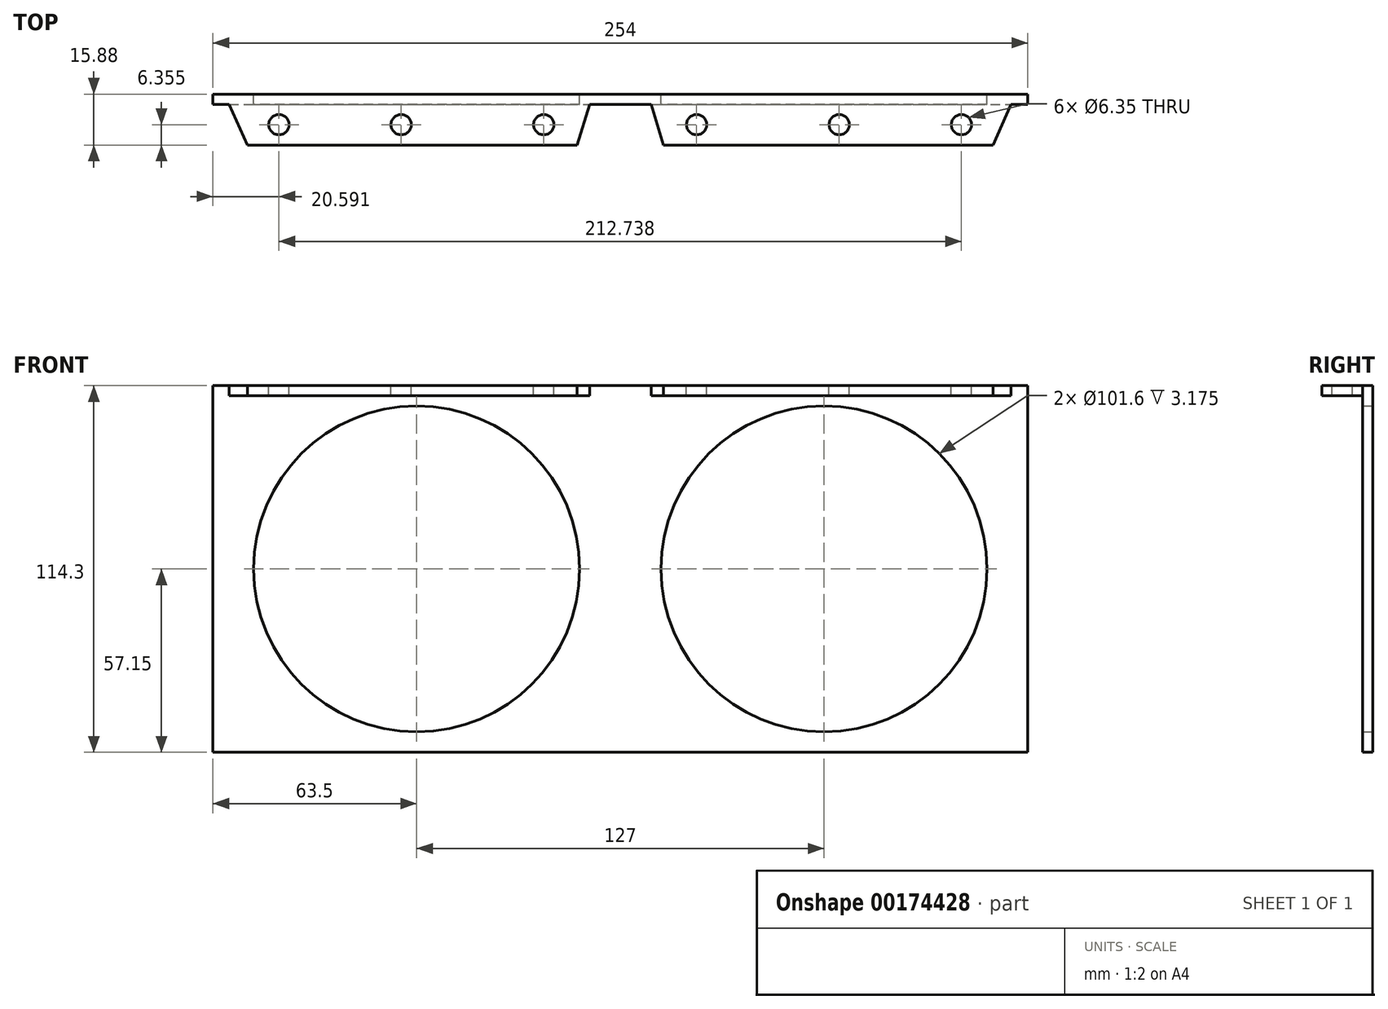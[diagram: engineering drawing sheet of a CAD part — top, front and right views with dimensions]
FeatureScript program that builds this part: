
annotation { "Feature Type Name" : "Feature", "Feature Type Description" : "" }
export const myFeature = defineFeature(function(context is Context, id is Id, definition is map)
    precondition{}
    {
        {
            var Q0;
            Q0=qCreatedBy(makeId("Front.planeOp"),FACE);
            var sketch = newSketch(context, id + "F0", { "sketchPlane" : qUnion([Q0])});
            skLineSegment(sketch, "E0.bottom", {"start": v(-127, -57.15) * mm, "end": v(127, -57.15) * mm});
            skLineSegment(sketch, "E0.top", {"start": v(-127, 57.15) * mm, "end": v(127, 57.15) * mm});
            skLineSegment(sketch, "E0.left", {"start": v(-127, -57.15) * mm, "end": v(-127, 57.15) * mm});
            skLineSegment(sketch, "E0.right", {"start": v(127, -57.15) * mm, "end": v(127, 57.15) * mm});
            skPoint(sketch, "E0.middle", {"position": v(0, 0) * mm});
            skCircle(sketch, "E1", {"center": v(63.5, 0) * mm, "radius": 50.8 * mm});
            skCircle(sketch, "E2", {"center": v(-63.5, 0) * mm, "radius": 50.8 * mm});
            skSolve(sketch);
        }
        {
            var Q0;
            Q0 = qSketchRegion(id + "F0", true);
            extrude(context, id + "F1", {"entities" : qUnion([Q0]), "depth" : 3.17 * mm});
        }
        {
            var Q0;
            Q0=makeQuery(id+"F1.opExtrude","CAP_FACE",FACE,{"disambiguationData":[OSD([sQuery(id+"F0.wireOp",EDGE,"E0.bottom"),sQuery(id+"F0.wireOp",EDGE,"E0.top"),sQuery(id+"F0.wireOp",EDGE,"E0.left"),sQuery(id+"F0.wireOp",EDGE,"E0.right"),sQuery(id+"F0.wireOp",EDGE,"E1"),sQuery(id+"F0.wireOp",EDGE,"E2")])],"isStart":false});
            var sketch = newSketch(context, id + "F2", { "sketchPlane" : qUnion([Q0])});
            skPoint(sketch, "E3", {"position": v(-122.01, 57.15) * mm});
            skPoint(sketch, "E4", {"position": v(-9.5, 57.15) * mm});
            skPoint(sketch, "E5", {"position": v(9.59, 57.15) * mm});
            skPoint(sketch, "E6", {"position": v(121.82, 57.15) * mm});
            skLineSegment(sketch, "E7.bottom", {"start": v(-122.01, 57.15) * mm, "end": v(-9.5, 57.15) * mm});
            skLineSegment(sketch, "E7.top", {"start": v(-122.01, 53.98) * mm, "end": v(-9.5, 53.98) * mm});
            skLineSegment(sketch, "E7.left", {"start": v(-122.01, 57.15) * mm, "end": v(-122.01, 53.98) * mm});
            skLineSegment(sketch, "E7.right", {"start": v(-9.5, 57.15) * mm, "end": v(-9.5, 53.98) * mm});
            skLineSegment(sketch, "E8.bottom", {"start": v(9.59, 57.15) * mm, "end": v(121.82, 57.15) * mm});
            skLineSegment(sketch, "E8.top", {"start": v(9.59, 53.98) * mm, "end": v(121.82, 53.98) * mm});
            skLineSegment(sketch, "E8.left", {"start": v(9.59, 57.15) * mm, "end": v(9.59, 53.98) * mm});
            skLineSegment(sketch, "E8.right", {"start": v(121.82, 57.15) * mm, "end": v(121.82, 53.98) * mm});
            skSolve(sketch);
        }
        {
            var Q0;
            Q0 = qSketchRegion(id + "F2", true);
            extrude(context, id + "F3", {"entities" : qUnion([Q0]), "operationType" : NewBodyOperationType.ADD, "depth" : 12.7 * mm, "offsetDistance" : 25.4 * mm});
        }
        {
            var Q0;
            Q0=makeQuery(id+"F3.boolean.opBoolean","MERGE",FACE,{"derivedFrom":[makeQuery(id+"F1.opExtrude","SWEPT_FACE",FACE,{"disambiguationData":[OSD([sQuery(id+"F0.wireOp",EDGE,"E0.top")])]}),makeQuery(id+"F3.opExtrude","SWEPT_FACE",FACE,{"disambiguationData":[OSD([sQuery(id+"F2.wireOp",EDGE,"E7.bottom")])]}),makeQuery(id+"F3.opExtrude","SWEPT_FACE",FACE,{"disambiguationData":[OSD([sQuery(id+"F2.wireOp",EDGE,"E8.bottom")])]})]});
            var sketch = newSketch(context, id + "F4", { "sketchPlane" : qUnion([Q0])});
            skLineSegment(sketch, "E9", {"start": v(-122.01, -3.18) * mm, "end": v(-116.2, -15.88) * mm});
            skLineSegment(sketch, "E10", {"start": v(-116.2, -15.88) * mm, "end": v(-122.01, -15.88) * mm});
            skLineSegment(sketch, "E11", {"start": v(-122.01, -15.88) * mm, "end": v(-122.01, -3.18) * mm});
            skLineSegment(sketch, "E12", {"start": v(-9.5, -3.18) * mm, "end": v(-13.46, -15.88) * mm});
            skLineSegment(sketch, "E13", {"start": v(-13.46, -15.88) * mm, "end": v(-9.5, -15.88) * mm});
            skLineSegment(sketch, "E14", {"start": v(-9.5, -15.88) * mm, "end": v(-9.5, -3.18) * mm});
            skLineSegment(sketch, "E15", {"start": v(9.59, -3.17) * mm, "end": v(13.48, -15.88) * mm});
            skLineSegment(sketch, "E16", {"start": v(13.48, -15.88) * mm, "end": v(9.59, -15.88) * mm});
            skLineSegment(sketch, "E17", {"start": v(9.59, -15.88) * mm, "end": v(9.59, -3.17) * mm});
            skLineSegment(sketch, "E18", {"start": v(121.82, -15.88) * mm, "end": v(116.24, -15.88) * mm});
            skLineSegment(sketch, "E19", {"start": v(116.24, -15.88) * mm, "end": v(121.82, -3.18) * mm});
            skLineSegment(sketch, "E20", {"start": v(121.82, -3.18) * mm, "end": v(121.82, -15.88) * mm});
            skSolve(sketch);
        }
        {
            var Q0;
            Q0 = qSketchRegion(id + "F4", true);
            extrude(context, id + "F5", {"entities" : qUnion([Q0]), "operationType" : NewBodyOperationType.REMOVE, "oppositeDirection" : true, "depth" : 25.4 * mm, "offsetDistance" : 25.4 * mm});
        }
        {
            var Q0;
            Q0=makeQuery(id+"F3.boolean.opBoolean","MERGE",FACE,{"derivedFrom":[makeQuery(id+"F1.opExtrude","SWEPT_FACE",FACE,{"disambiguationData":[OSD([sQuery(id+"F0.wireOp",EDGE,"E0.top")])]}),makeQuery(id+"F3.opExtrude","SWEPT_FACE",FACE,{"disambiguationData":[OSD([sQuery(id+"F2.wireOp",EDGE,"E7.bottom")])]}),makeQuery(id+"F3.opExtrude","SWEPT_FACE",FACE,{"disambiguationData":[OSD([sQuery(id+"F2.wireOp",EDGE,"E8.bottom")])]})]});
            var sketch = newSketch(context, id + "F6", { "sketchPlane" : qUnion([Q0])});
            skLineSegment(sketch, "E21", {"start": v(-119.1, -9.53) * mm, "end": v(119.03, -9.53) * mm});
            skCircle(sketch, "E22", {"center": v(-106.4, -9.53) * mm, "radius": 3.18 * mm});
            skCircle(sketch, "E23", {"center": v(-68.3, -9.53) * mm, "radius": 3.18 * mm});
            skCircle(sketch, "E24", {"center": v(-23.86, -9.53) * mm, "radius": 3.18 * mm});
            skCircle(sketch, "E25", {"center": v(68.23, -9.53) * mm, "radius": 3.18 * mm});
            skCircle(sketch, "E26", {"center": v(106.33, -9.53) * mm, "radius": 3.18 * mm});
            skCircle(sketch, "E27", {"center": v(23.78, -9.53) * mm, "radius": 3.18 * mm});
            skSolve(sketch);
        }
        {
            var Q0;
            Q0 = qSketchRegion(id + "F6", true);
            extrude(context, id + "F7", {"entities" : qUnion([Q0]), "operationType" : NewBodyOperationType.REMOVE, "oppositeDirection" : true, "depth" : 25.4 * mm, "offsetDistance" : 25.4 * mm});
        }
    });
